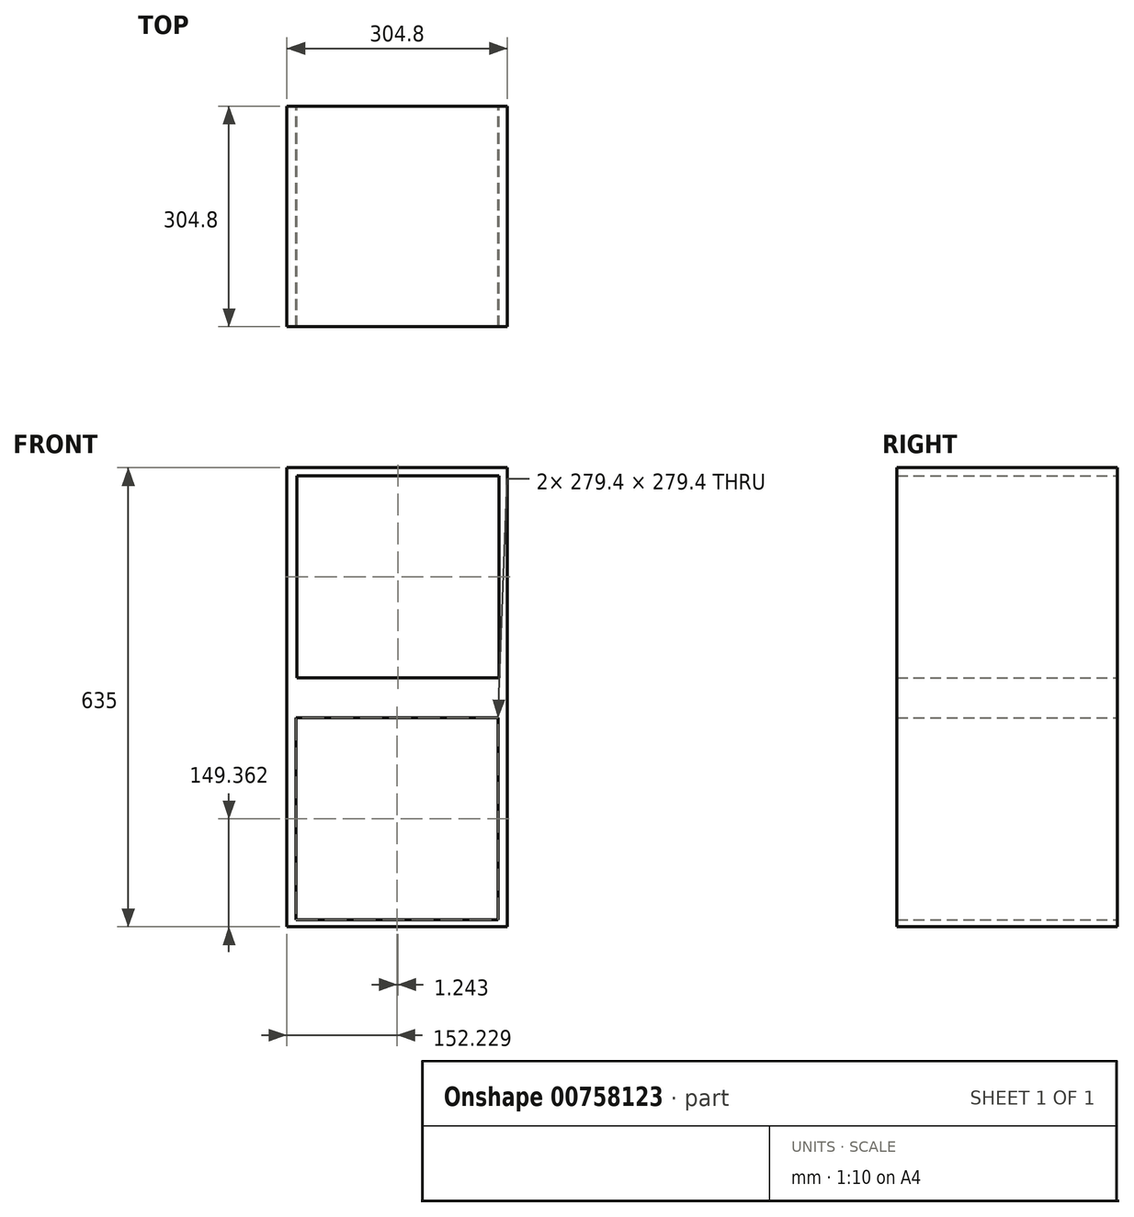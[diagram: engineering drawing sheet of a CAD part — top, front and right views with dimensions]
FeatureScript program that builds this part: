
annotation { "Feature Type Name" : "Feature", "Feature Type Description" : "" }
export const myFeature = defineFeature(function(context is Context, id is Id, definition is map)
    precondition{}
    {
        {
            var Q0;
            Q0=qCreatedBy(makeId("Front.planeOp"),FACE);
            var sketch = newSketch(context, id + "F0", { "sketchPlane" : qUnion([Q0])});
            skLineSegment(sketch, "E0.bottom", {"start": v(-244.24, 159.33) * mm, "end": v(60.56, 159.33) * mm});
            skLineSegment(sketch, "E0.top", {"start": v(-244.24, -475.67) * mm, "end": v(60.56, -475.67) * mm});
            skLineSegment(sketch, "E0.left", {"start": v(-244.24, 159.33) * mm, "end": v(-244.24, -475.67) * mm});
            skLineSegment(sketch, "E0.right", {"start": v(60.56, 159.33) * mm, "end": v(60.56, -475.67) * mm});
            skLineSegment(sketch, "E1", {"start": v(-244.24, -475.67) * mm, "end": v(-244.24, -170.87) * mm});
            skLineSegment(sketch, "E2", {"start": v(-244.24, 159.33) * mm, "end": v(-244.24, -145.47) * mm});
            skLineSegment(sketch, "E3.bottom", {"start": v(-244.24, -145.47) * mm, "end": v(60.56, -145.47) * mm});
            skLineSegment(sketch, "E3.top", {"start": v(-244.24, -170.87) * mm, "end": v(60.56, -170.87) * mm});
            skLineSegment(sketch, "E3.left", {"start": v(-244.24, -145.47) * mm, "end": v(-244.24, -170.87) * mm});
            skLineSegment(sketch, "E3.right", {"start": v(60.56, -145.47) * mm, "end": v(60.56, -170.87) * mm});
            skLineSegment(sketch, "E4.bottom", {"start": v(-230.47, 147.96) * mm, "end": v(48.93, 147.96) * mm});
            skLineSegment(sketch, "E4.top", {"start": v(-230.47, -131.44) * mm, "end": v(48.93, -131.44) * mm});
            skLineSegment(sketch, "E4.left", {"start": v(-230.47, 147.96) * mm, "end": v(-230.47, -131.44) * mm});
            skLineSegment(sketch, "E4.right", {"start": v(48.93, 147.96) * mm, "end": v(48.93, -131.44) * mm});
            skLineSegment(sketch, "E5.bottom", {"start": v(-231.71, -186.6) * mm, "end": v(47.69, -186.6) * mm});
            skLineSegment(sketch, "E5.top", {"start": v(-231.71, -466) * mm, "end": v(47.69, -466) * mm});
            skLineSegment(sketch, "E5.left", {"start": v(-231.71, -186.6) * mm, "end": v(-231.71, -466) * mm});
            skLineSegment(sketch, "E5.right", {"start": v(47.69, -186.6) * mm, "end": v(47.69, -466) * mm});
            skSolve(sketch);
        }
        {
            var Q0;
            Q0 = qSketchRegion(id + "F0", true);
            extrude(context, id + "F1", {"entities" : qUnion([Q0]), "depth" : 304.8 * mm, "offsetDistance" : 25.4 * mm});
        }
    });
